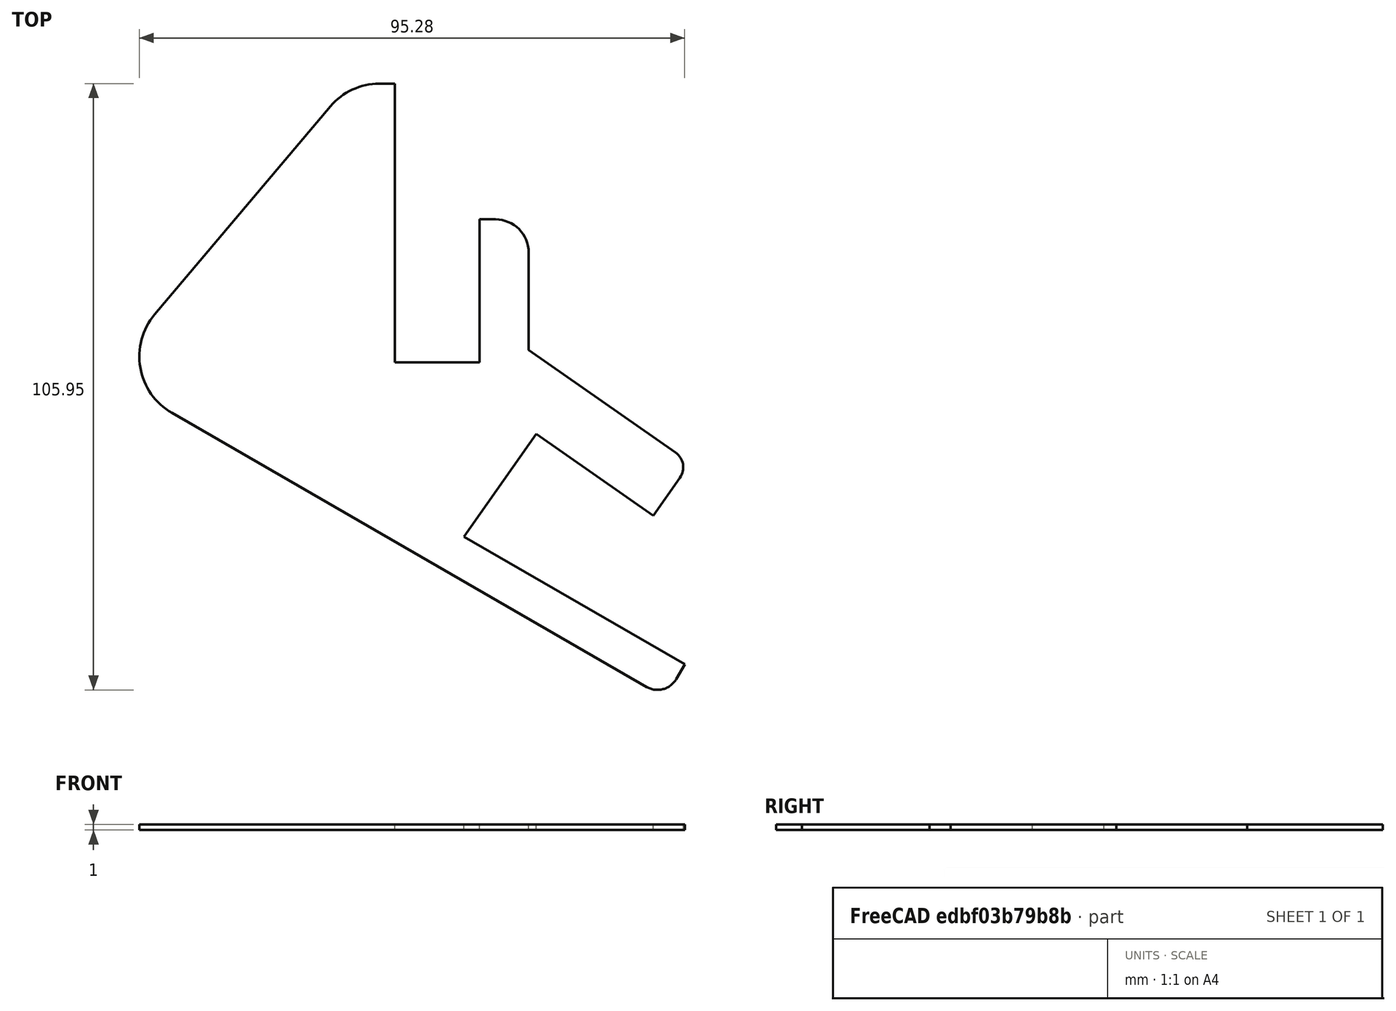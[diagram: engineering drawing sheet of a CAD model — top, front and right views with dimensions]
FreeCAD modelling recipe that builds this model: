
FCSTD DOCUMENT  (FreeCAD 0.14R3702 (Git))
Label: dock_tableta
License: CC-BY 3.0
LicenseURL: http://creativecommons.org/licenses/by/3.0/
objects: Sketcher::SketchObject×1, PartDesign::Pad×1
note: 3 computed .brp shape members not serialized (recipe doc carries the construction recipe); baked Part::Feature solids carry a one-line shape summary decoded from their .brp

FEATURE [Sketcher::SketchObject] Sketch
  sketch-geometry (19):
    g0: LineSegment StartX=-10.1604 StartY=55.7137 StartZ=0 EndX=-7.4 EndY=55.7137 EndZ=0
    g1: LineSegment StartX=-7.4 StartY=55.7137 StartZ=0 EndX=-7.4 EndY=7.00116 EndZ=0
    g2: LineSegment StartX=-7.4 StartY=7.00116 StartZ=0 EndX=7.4 EndY=7.00116 EndZ=0
    g3: LineSegment StartX=7.4 StartY=7.00116 StartZ=0 EndX=7.4 EndY=32.0012 EndZ=0
    g4: LineSegment StartX=7.4 StartY=32.0012 StartZ=0 EndX=10.1604 EndY=32.0012 EndZ=0
    g5: LineSegment StartX=15.9719 StartY=26.1896 StartZ=0 EndX=15.9719 EndY=9.18934 EndZ=0
    g6: LineSegment StartX=15.9719 StartY=9.18934 StartZ=0 EndX=41.6105 EndY=-8.76299 EndZ=0
    g7: LineSegment StartX=42.3874 StartY=-13.1694 StartZ=0 EndX=37.7339 EndY=-19.8154 EndZ=0
    g8: LineSegment StartX=37.7339 StartY=-19.8154 StartZ=0 EndX=17.2551 EndY=-5.47594 EndZ=0
    g9: LineSegment StartX=17.2551 StartY=-5.47594 StartZ=0 EndX=4.63642 EndY=-23.4973 EndZ=0
    g10: LineSegment StartX=4.63642 StartY=-23.4973 StartZ=0 EndX=43.2231 EndY=-45.7753 EndZ=0
    g11: LineSegment StartX=43.2231 StartY=-45.7753 StartZ=0 EndX=41.7349 EndY=-48.353 EndZ=0
    g12: LineSegment StartX=36.5877 StartY=-49.7321 StartZ=0 EndX=-46.3671 EndY=-1.83814 EndZ=0
    g13: LineSegment StartX=-49.376 StartY=15.3698 StartZ=0 EndX=-18.6584 EndY=51.7658 EndZ=0
    g14: ArcOfCircle CenterX=-40.6729 CenterY=8.02454 CenterZ=0 NormalX=0 NormalY=0 NormalZ=1 Radius=11.3884 StartAngle=2.4406 EndAngle=4.18879
    g15: ArcOfCircle CenterX=-10.1604 CenterY=44.5936 CenterZ=0 NormalX=0 NormalY=0 NormalZ=1 Radius=11.1202 StartAngle=1.5708 EndAngle=2.4406
    g16: ArcOfCircle CenterX=10.1604 CenterY=26.1896 CenterZ=0 NormalX=0 NormalY=0 NormalZ=1 Radius=5.81152 StartAngle=0 EndAngle=1.5708
    g17: ArcOfCircle CenterX=39.7957 CenterY=-11.3547 CenterZ=0 NormalX=0 NormalY=0 NormalZ=1 Radius=3.16387 StartAngle=5.67232 EndAngle=7.24312
    g18: ArcOfCircle CenterX=38.4717 CenterY=-46.469 CenterZ=0 NormalX=0 NormalY=0 NormalZ=1 Radius=3.768 StartAngle=4.18879 EndAngle=5.75959
  constraints (38):
    c: Horizontal(g0)
    c: Coincident(g0,g1)
    c: Vertical(g1)
    c: Coincident(g1,g2)
    c: Horizontal(g2)
    c: Coincident(g2,g3)
    c: Vertical(g3)
    c: Coincident(g3,g4)
    c: Horizontal(g4)
    c: Vertical(g5)
    c: Coincident(g5,g6)
    c: Coincident(g7,g8)
    c: Coincident(g8,g9)
    c: Coincident(g9,g10)
    c: Coincident(g10,g11)
    c: Equal(g0,g4)
    c: Symmetric(g1,g2,g-2)
    c: Perpendicular(g6,g7)
    c: Parallel(g6,g8)
    c: Distance(g9) = 22
    c: Distance(g2) = 14.8
    c: Distance(g3) = 25
    c: Parallel(g10,g12)
    c: Perpendicular(g12,g11)
    c: Perpendicular(g8,g9)
    c: Angle(g10,g9) = 1.48353
    c: Distance(g8) = 25
    c: Angle(g6,g5) = 2.18166
    c: Tangent(g13,g14)
    c: Tangent(g12,g14)
    c: Tangent(g13,g15)
    c: Tangent(g0,g15)
    c: Tangent(g4,g16)
    c: Tangent(g5,g16)
    c: Tangent(g6,g17)
    c: Tangent(g7,g17)
    c: Tangent(g12,g18)
    c: Tangent(g11,g18)
FEATURE [PartDesign::Pad] Pad
  Length = 1
  Length2 = 100
  Sketch = -> Sketch
  Type = 0
